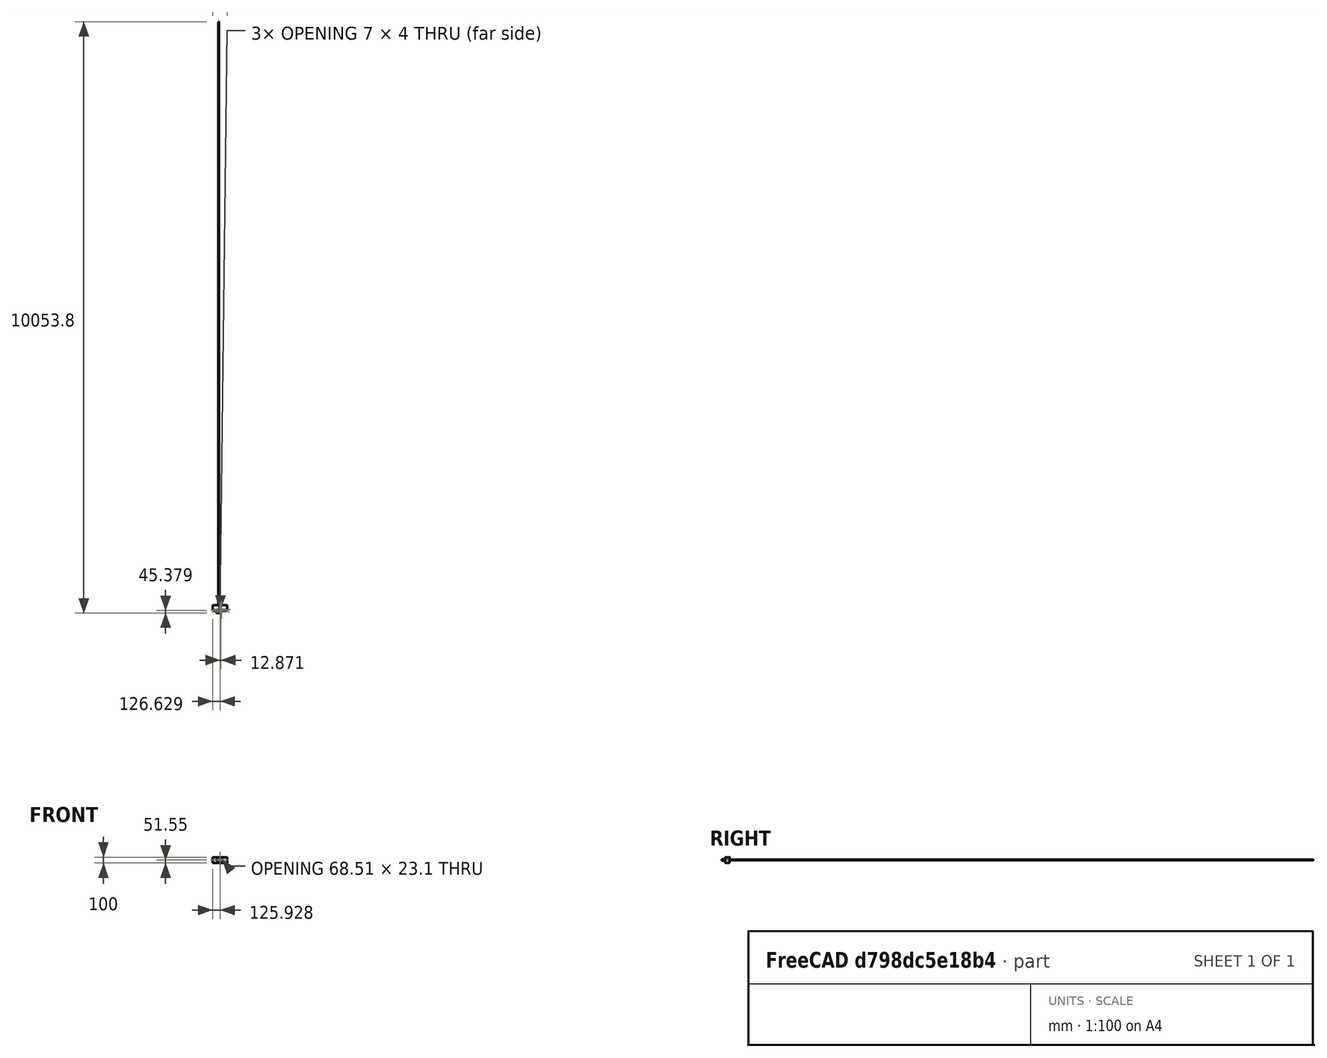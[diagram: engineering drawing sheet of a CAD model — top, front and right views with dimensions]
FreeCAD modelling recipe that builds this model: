
FCSTD DOCUMENT  (FreeCAD 0.16R5861 (Git))
Label: flexystruder_body_holder
License: CreativeCommons Attribution-ShareAlike
LicenseURL: http://creativecommons.org/licenses/by-sa/4.0/
objects: Sketcher::SketchObject×6, Part::Feature×4, PartDesign::Pocket×4, PartDesign::Pad×2, Mesh::Feature×1, PartDesign::Fillet×1, Part::Cut×1
note: 24 computed .brp shape members not serialized (recipe doc carries the construction recipe); baked Part::Feature solids carry a one-line shape summary decoded from their .brp

FEATURE [Mesh::Feature] flexystruder_body_hex_v2_0  label="flexystruder_body_hex_v2.0"
FEATURE [Part::Feature] flexystruder_body_hex_v2_0001
  shape: bbox 97.06 x 64.55 x 27.5 mm, 7934 faces, 0 solids (baked)
FEATURE [Part::Feature] flexystruder_body_hex_v2_0001001  label="flexystruder_body_hex_v2_0002"
  shape: bbox 97.06 x 64.55 x 27.5 mm, 4378 faces, 0 solids (baked)
FEATURE [Part::Feature] flexystruder_body_hex_v2_0001001_solid  label="flexystruder_body_hex_v2_0002 (Solid)"
  shape: bbox 97.06 x 64.55 x 27.5 mm, 4378 faces (baked)
FEATURE [Sketcher::SketchObject] Sketch
  Placement = pos=(0,0,0) rot=(0.57735,0.57735,0.57735;2.0944rad)
  sketch-geometry (4):
    g0: LineSegment StartX=53.7731 StartY=-40 StartZ=0 EndX=132 EndY=-40 EndZ=0
    g1: LineSegment StartX=132 StartY=-40 StartZ=0 EndX=132 EndY=60 EndZ=0
    g2: LineSegment StartX=132 StartY=60 StartZ=0 EndX=53.7731 EndY=60 EndZ=0
    g3: LineSegment StartX=53.7731 StartY=60 StartZ=0 EndX=53.7731 EndY=-40 EndZ=0
  constraints (10):
    c: Coincident(g0,g1)
    c: Coincident(g1,g2)
    c: Coincident(g2,g3)
    c: Coincident(g3,g0)
    c: Horizontal(g0)
    c: Horizontal(g2)
    c: Vertical(g1)
    c: Vertical(g3)
    c: DistanceY(g1) = 100
    c: DistanceY(g-1,g0) = -40
FEATURE [PartDesign::Pad] Pad
  Length = 150
  Length2 = 100
  Placement = pos=(0,0,0) rot=(0.57735,0.57735,0.57735;2.0944rad)
  Sketch = -> Sketch
  Type = 4
FEATURE [PartDesign::Fillet] Fillet
  Base = -> Pad [Edge8,Edge1,Edge12,Edge11,Edge10,Edge4,Edge9,Edge3]
  Placement = pos=(0,0,0) rot=(0.57735,0.57735,0.57735;2.0944rad)
  Radius = 10
FEATURE [Sketcher::SketchObject] Sketch001
  Placement = pos=(0,0,0) rot=(1,0,0;3.14159rad)
  Support = -> flexystruder_body_hex_v2_0001001_solid [Face1922]
  sketch-geometry (4):
    g0: ArcOfCircle CenterX=52 CenterY=-58.243 CenterZ=0 NormalX=0 NormalY=0 NormalZ=1 Radius=4.06074 StartAngle=1.5708 EndAngle=4.71239
    g1: ArcOfCircle CenterX=56.5198 CenterY=-58.243 CenterZ=0 NormalX=0 NormalY=0 NormalZ=1 Radius=4.06074 StartAngle=4.71239 EndAngle=7.85398
    g2: LineSegment StartX=52 StartY=-62.3037 StartZ=0 EndX=56.5198 EndY=-62.3037 EndZ=0
    g3: LineSegment StartX=52 StartY=-54.1822 StartZ=0 EndX=56.5198 EndY=-54.1822 EndZ=0
  constraints (6):
    c: Tangent(g0,g3) = 1.5708
    c: Tangent(g0,g2) = -1.5708
    c: Tangent(g2,g1) = -1.5708
    c: Tangent(g3,g1) = 1.5708
    c: Horizontal(g2)
    c: Equal(g0,g1)
FEATURE [PartDesign::Pad] Pad001
  Length = 9.5
  Length2 = 100
  Reversed = true
  Sketch = -> Sketch001
  Type = 0
FEATURE [Part::Cut] Cut
  Base = -> Fillet
  Tool = -> Pad001
FEATURE [Sketcher::SketchObject] Sketch002
  Placement = pos=(0,53.7731,0) rot=(1,0,0;1.5708rad)
  Support = -> Cut [Face403]
  sketch-geometry (1):
    g0: Circle CenterX=0.482362 CenterY=14 CenterZ=0 NormalX=0 NormalY=0 NormalZ=1 Radius=5
  constraints (1):
    c: Radius(g0) = 5
FEATURE [PartDesign::Pocket] Pocket
  Length = 5
  Sketch = -> Sketch002
  Type = 1
FEATURE [Part::Feature] Pocket001
  shape: bbox 250 x 78.23 x 100 mm, 1139 faces (baked)
FEATURE [Sketcher::SketchObject] Sketch003
  ExternalGeometry = -> [Pocket001]
  Placement = pos=(0,53.7731,0) rot=(1,0,0;1.5708rad)
  Support = -> Pocket001 [Face62]
  sketch-geometry (4):
    g0: LineSegment StartX=44.0071 StartY=0 StartZ=0 EndX=51.0275 EndY=0 EndZ=0
    g1: LineSegment StartX=51.0275 StartY=0 StartZ=0 EndX=51.0275 EndY=1.89901 EndZ=0
    g2: LineSegment StartX=51.0275 StartY=1.89901 StartZ=0 EndX=44.0071 EndY=1.89901 EndZ=0
    g3: LineSegment StartX=44.0071 StartY=1.89901 StartZ=0 EndX=44.0071 EndY=0 EndZ=0
  constraints (9):
    c: Coincident(g0,g1)
    c: Coincident(g1,g2)
    c: Coincident(g2,g3)
    c: Coincident(g3,g0)
    c: Horizontal(g0)
    c: Horizontal(g2)
    c: Vertical(g1)
    c: Vertical(g3)
    c: Coincident(g0,g-4)
FEATURE [PartDesign::Pocket] Pocket002
  Length = 5
  Sketch = -> Sketch003
  Type = 0
FEATURE [Sketcher::SketchObject] Sketch004
  ExternalGeometry = -> [Pocket002]
  Placement = pos=(0,53.7731,0) rot=(1,0,0;1.5708rad)
  Support = -> Pocket002 [Face6]
  sketch-geometry (4):
    g0: LineSegment StartX=59.4175 StartY=0 StartZ=0 EndX=62 EndY=0 EndZ=0
    g1: LineSegment StartX=62 StartY=0 StartZ=0 EndX=62 EndY=9.5 EndZ=0
    g2: LineSegment StartX=62 StartY=9.5 StartZ=0 EndX=59.4175 EndY=9.5 EndZ=0
    g3: LineSegment StartX=59.4175 StartY=9.5 StartZ=0 EndX=59.4175 EndY=0 EndZ=0
  constraints (10):
    c: Coincident(g0,g1)
    c: Coincident(g1,g2)
    c: Coincident(g2,g3)
    c: Coincident(g3,g0)
    c: Horizontal(g0)
    c: Horizontal(g2)
    c: Vertical(g1)
    c: Vertical(g3)
    c: Coincident(g0,g-4)
    c: PointOnObject(g2,g-3)
FEATURE [PartDesign::Pocket] Pocket003
  Length = 6
  Sketch = -> Sketch004
  Type = 0
FEATURE [Sketcher::SketchObject] Sketch005
  Placement = pos=(0,53.7731,0) rot=(1,0,0;1.5708rad)
  Support = -> Pocket003 [Face6]
  sketch-geometry (4):
    g0: LineSegment StartX=-9 StartY=23.4478 StartZ=0 EndX=62.6602 EndY=23.4478 EndZ=0
    g1: LineSegment StartX=62.6602 StartY=23.4478 StartZ=0 EndX=62.6602 EndY=-0.539133 EndZ=0
    g2: LineSegment StartX=62.6602 StartY=-0.539133 StartZ=0 EndX=-9 EndY=-0.539133 EndZ=0
    g3: LineSegment StartX=-9 StartY=-0.539133 StartZ=0 EndX=-9 EndY=23.4478 EndZ=0
  constraints (8):
    c: Coincident(g0,g1)
    c: Coincident(g1,g2)
    c: Coincident(g2,g3)
    c: Coincident(g3,g0)
    c: Horizontal(g0)
    c: Horizontal(g2)
    c: Vertical(g1)
    c: Vertical(g3)
FEATURE [PartDesign::Pocket] Pocket004
  Length = 1
  Sketch = -> Sketch005
  Type = 0
